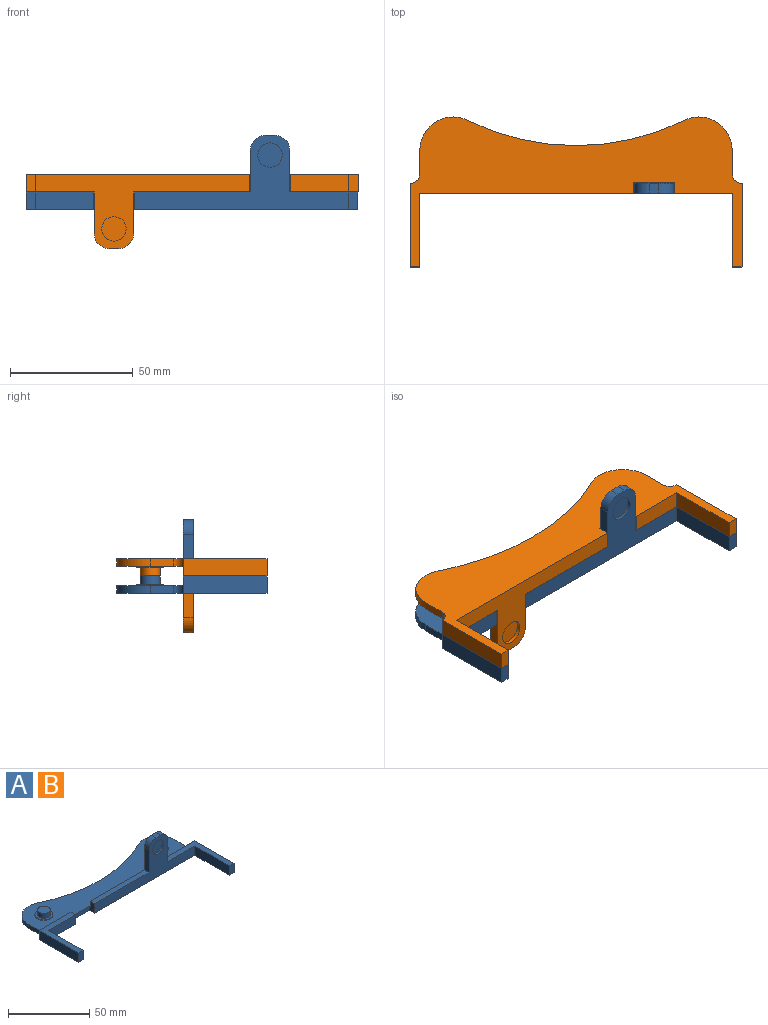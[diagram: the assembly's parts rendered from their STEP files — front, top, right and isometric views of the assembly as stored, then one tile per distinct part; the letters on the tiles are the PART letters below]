
ASSEMBLY  parts=2 mates=1
PART A: 42 faces, bbox 135x61x30 mm
  f0: plane 34x27.76mm, normal (0,0,1), area 231mm2, adj f1,f8,f25,f26,f27,f36
  f1: plane 86.99x30mm, normal (0,-1,0), area 884.5mm2, adj f0,f2,f9,f25,f32,f35,f36,f37
  f2: plane 135x60.99mm, normal (0,0,-1), area 3325.7mm2, adj f1,f3,f5,f6,f8,f18,f19,f20
  f3: plane 27.51x7mm, normal (0,1,0), area 110.1mm2, adj f2,f4,f7,f28,f30,f33
  f4: plane 34x27.51mm, normal (0,0,1), area 230mm2, adj f3,f23,f24,f28,f29,f33
  f5: plane 9.49x3mm, normal (-1,0,0), area 28.5mm2, adj f2,f7,f19,f30
  f6: plane 9.49x3mm, normal (1,0,0), area 28.5mm2, adj f2,f7,f18,f31
  f7: plane 134.98x26.99mm, normal (0,0,1), area 2421.7mm2, adj f3,f5,f6,f8,f10,f12,f18,f19
  f8: plane 90.99x30mm, normal (0,1,0), area 716.6mm2, adj f0,f2,f7,f9,f27,f31,f32,f35
  f9: plane 47.24x4mm, normal (0,0,1), area 189mm2, adj f1,f8,f32,f35
  f10: cylinder r=5.5mm len=11mm, axis (0,0,-1), area 17.3mm2, adj f7,f11
  f11: plane 11x11mm, normal (0,0,1), area 44.8mm2, adj f10,f14
  f12: cylinder r=5.5mm len=11mm, axis (0,0,-1), area 17.3mm2, adj f7,f13
  f13: plane 11x11mm, normal (0,0,1), area 44.8mm2, adj f12,f16
  f14: cylinder r=4mm len=8mm, axis (0,0,-1), area 88mm2, adj f11,f15
  f15: plane 8x8mm, normal (0,0,1), area 50.3mm2, adj f14
  f16: cylinder r=4mm len=8mm, axis (0,0,-1), area 88mm2, adj f13,f17
  f17: plane 8x8mm, normal (0,0,1), area 50.3mm2, adj f16
  f18: cylinder r=13.5mm len=13.5mm, axis (0,0,-1), area 63.6mm2, adj f2,f6,f7,f21
  f19: cylinder r=13.5mm len=13.5mm, axis (0,0,1), area 63.6mm2, adj f2,f5,f7,f22
  f20: cylinder r=99.98mm len=88.18mm, axis (0,0,1), area 274mm2, adj f2,f7,f21,f22
  f21: cylinder r=13.5mm len=5.9mm, axis (0,0,1), area 18.3mm2, adj f2,f7,f18,f20
  f22: cylinder r=13.5mm len=5.9mm, axis (0,0,-1), area 18.3mm2, adj f2,f7,f19,f20
  f23: plane 30x7mm, normal (1,0,0), area 210mm2, adj f2,f4,f24,f29
  f24: plane 23.51x7mm, normal (0,-1,0), area 164.5mm2, adj f2,f4,f23,f33
  f25: plane 30x7mm, normal (-1,0,0), area 210mm2, adj f0,f1,f2,f26
  f26: plane 7x4mm, normal (0,-1,0), area 28mm2, adj f0,f2,f25,f27
  f27: plane 34x7mm, normal (1,0,0), area 238mm2, adj f0,f2,f8,f26
  f28: plane 34x7mm, normal (-1,0,0), area 238mm2, adj f2,f3,f4,f29
  f29: plane 7x4mm, normal (0,-1,0), area 28mm2, adj f2,f4,f23,f28
  f30: cylinder r=4mm len=4mm, axis (0,0,-1), area 18.8mm2, adj f2,f3,f5,f7
  f31: cylinder r=4mm len=4mm, axis (0,0,1), area 18.8mm2, adj f2,f6,f7,f8
  f32: plane 7x4.5mm, normal (-1,0,0), area 29.5mm2, adj f1,f2,f7,f8,f9,f34
  f33: plane 7x4.5mm, normal (1,0,0), area 29.5mm2, adj f2,f3,f4,f7,f24,f34
  f34: plane 16.5x3mm, normal (0,-1,0), area 49.5mm2, adj f2,f7,f32,f33
  f35: plane 17x4mm, normal (-1,0,0), area 68mm2, adj f1,f8,f9,f40
  f36: plane 17x4mm, normal (1,0,0), area 68mm2, adj f0,f1,f8,f41
  f37: plane 4x4mm, normal (0,0,1), area 16mm2, adj f1,f8,f40,f41
  f38: cylinder r=4.95mm len=9.9mm, axis (0,-1,0), area 46.7mm2, adj f1,f39
  f39: plane 9.9x9.9mm, normal (0,-1,0), area 77mm2, adj f38
  f40: cylinder r=6mm len=6mm, axis (0,-1,0), area 37.7mm2, adj f1,f8,f35,f37
  f41: cylinder r=6mm len=6mm, axis (0,1,0), area 37.7mm2, adj f1,f8,f36,f37
PART B: same geometry as A
PLACE A t=(82.99,37.05,1.55)mm
PLACE B rot(axis=(0,1,0),180deg) t=(209.96,37.05,9.55)mm
MATE fastened B.f10 <-> A.f12  axis (0,0,-1) through (196.46,50.55,5.55)mm
